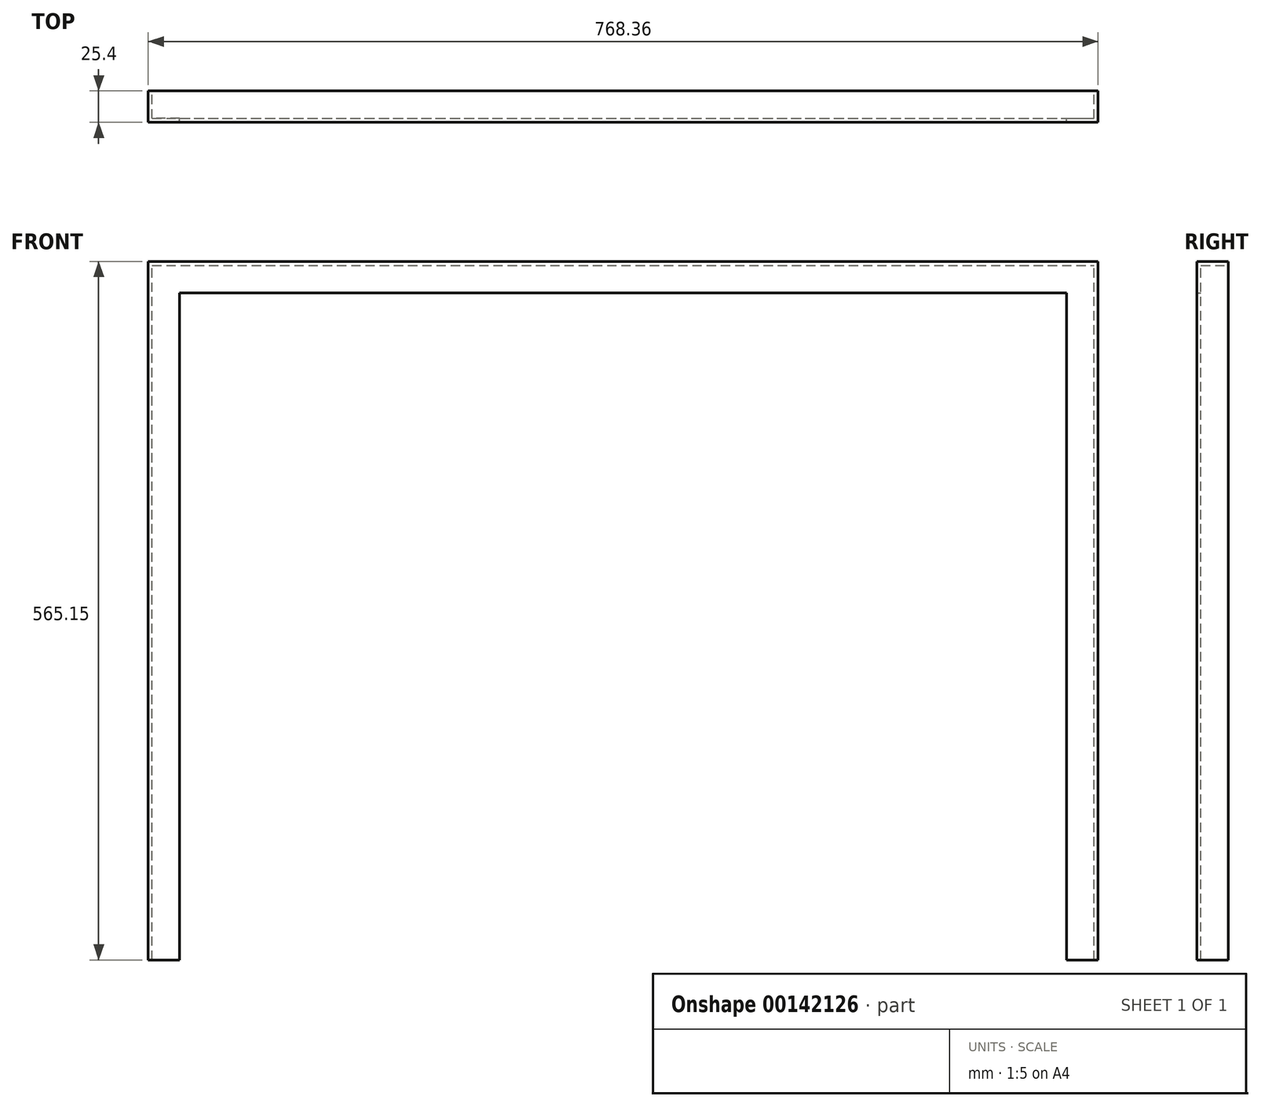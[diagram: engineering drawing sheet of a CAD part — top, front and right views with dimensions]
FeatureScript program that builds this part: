
annotation { "Feature Type Name" : "Feature", "Feature Type Description" : "" }
export const myFeature = defineFeature(function(context is Context, id is Id, definition is map)
    precondition{}
    {
        {
            var Q0;
            Q0=qCreatedBy(makeId("Top.planeOp"),FACE);
            var sketch = newSketch(context, id + "F0", { "sketchPlane" : qUnion([Q0])});
            skLineSegment(sketch, "E0.bottom", {"start": v(384.18, -12.7) * mm, "end": v(-384.18, -12.7) * mm});
            skLineSegment(sketch, "E0.top", {"start": v(384.18, 12.7) * mm, "end": v(-384.18, 12.7) * mm});
            skLineSegment(sketch, "E0.left", {"start": v(384.18, -12.7) * mm, "end": v(384.18, 12.7) * mm});
            skLineSegment(sketch, "E0.right", {"start": v(-384.18, -12.7) * mm, "end": v(-384.18, 12.7) * mm});
            skPoint(sketch, "E0.middle", {"position": v(0, 0) * mm});
            skSolve(sketch);
        }
        {
            var Q0;
            Q0=makeQuery(id+"F0.imprint","IMPRINT",FACE,{"disambiguationData":[TD([[makeQuery(id+"F0.imprint","IMPRINT",EDGE,{"derivedFrom":sQuery(id+"F0.wireOp",EDGE,"E0.bottom")}),-1.0]])]});
            extrude(context, id + "F1", {"entities" : qUnion([Q0]), "depth" : 25.4 * mm});
        }
        {
            var Q0;
            Q0=makeQuery(id+"F1.opExtrude","SWEPT_FACE",FACE,{"disambiguationData":[OSD([sQuery(id+"F0.wireOp",EDGE,"E0.left")])]});
            var sketch = newSketch(context, id + "F2", { "sketchPlane" : qUnion([Q0])});
            skLineSegment(sketch, "E1.bottom", {"start": v(12.7, 0) * mm, "end": v(-9.52, 0) * mm});
            skLineSegment(sketch, "E1.top", {"start": v(12.7, 22.23) * mm, "end": v(-9.52, 22.23) * mm});
            skLineSegment(sketch, "E1.left", {"start": v(12.7, 0) * mm, "end": v(12.7, 22.22) * mm});
            skLineSegment(sketch, "E1.right", {"start": v(-9.52, 0) * mm, "end": v(-9.52, 22.23) * mm});
            skSolve(sketch);
        }
        {
            var Q0;
            Q0=makeQuery(id+"F2.imprint","IMPRINT",FACE,{"disambiguationData":[TD([[makeQuery(id+"F2.imprint","IMPRINT",EDGE,{"derivedFrom":sQuery(id+"F2.wireOp",EDGE,"E1.bottom")}),1.0]])]});
            extrude(context, id + "F3", {"entities" : qUnion([Q0]), "operationType" : NewBodyOperationType.REMOVE, "endBound" : BoundingType.THROUGH_ALL, "oppositeDirection" : true, "depth" : 25.4 * mm});
        }
        {
            var Q0;
            Q0=makeQuery(id+"F1.opExtrude","CAP_FACE",FACE,{"disambiguationData":[OSD([sQuery(id+"F0.wireOp",EDGE,"E0.bottom"),sQuery(id+"F0.wireOp",EDGE,"E0.top"),sQuery(id+"F0.wireOp",EDGE,"E0.left"),sQuery(id+"F0.wireOp",EDGE,"E0.right")])],"isStart":false});
            var sketch = newSketch(context, id + "F4", { "sketchPlane" : qUnion([Q0])});
            skLineSegment(sketch, "E2", {"start": v(384.18, 12.7) * mm, "end": v(384.18, -12.7) * mm});
            skLineSegment(sketch, "E3", {"start": v(384.18, -12.7) * mm, "end": v(358.78, -12.7) * mm});
            skLineSegment(sketch, "E4", {"start": v(358.78, -12.7) * mm, "end": v(358.78, -9.53) * mm});
            skLineSegment(sketch, "E5", {"start": v(358.78, -9.52) * mm, "end": v(381, -9.52) * mm});
            skLineSegment(sketch, "E6", {"start": v(381, -9.53) * mm, "end": v(381, 12.7) * mm});
            skLineSegment(sketch, "E7", {"start": v(381, 12.7) * mm, "end": v(384.18, 12.7) * mm});
            skSolve(sketch);
        }
        {
            var Q0;
            Q0 = qSketchRegion(id + "F4", true);
            extrude(context, id + "F5", {"entities" : qUnion([Q0]), "operationType" : NewBodyOperationType.ADD, "oppositeDirection" : true, "depth" : 565.15 * mm});
        }
        {
            var Q0;
            Q0=makeQuery(id+"F1.opExtrude","SWEPT_BODY",BODY,{"disambiguationData":[OSD([sQuery(id+"F0.wireOp",EDGE,"E0.bottom"),sQuery(id+"F0.wireOp",EDGE,"E0.top"),sQuery(id+"F0.wireOp",EDGE,"E0.left"),sQuery(id+"F0.wireOp",EDGE,"E0.right")])]});
            var Q1;
            Q1=qCreatedBy(makeId("Right.planeOp"),FACE);
            mirror(context, id + "F6", {"operationType" : NewBodyOperationType.ADD, "entities" : qUnion([Q0]), "mirrorPlane" : qUnion([Q1])});
        }
    });
